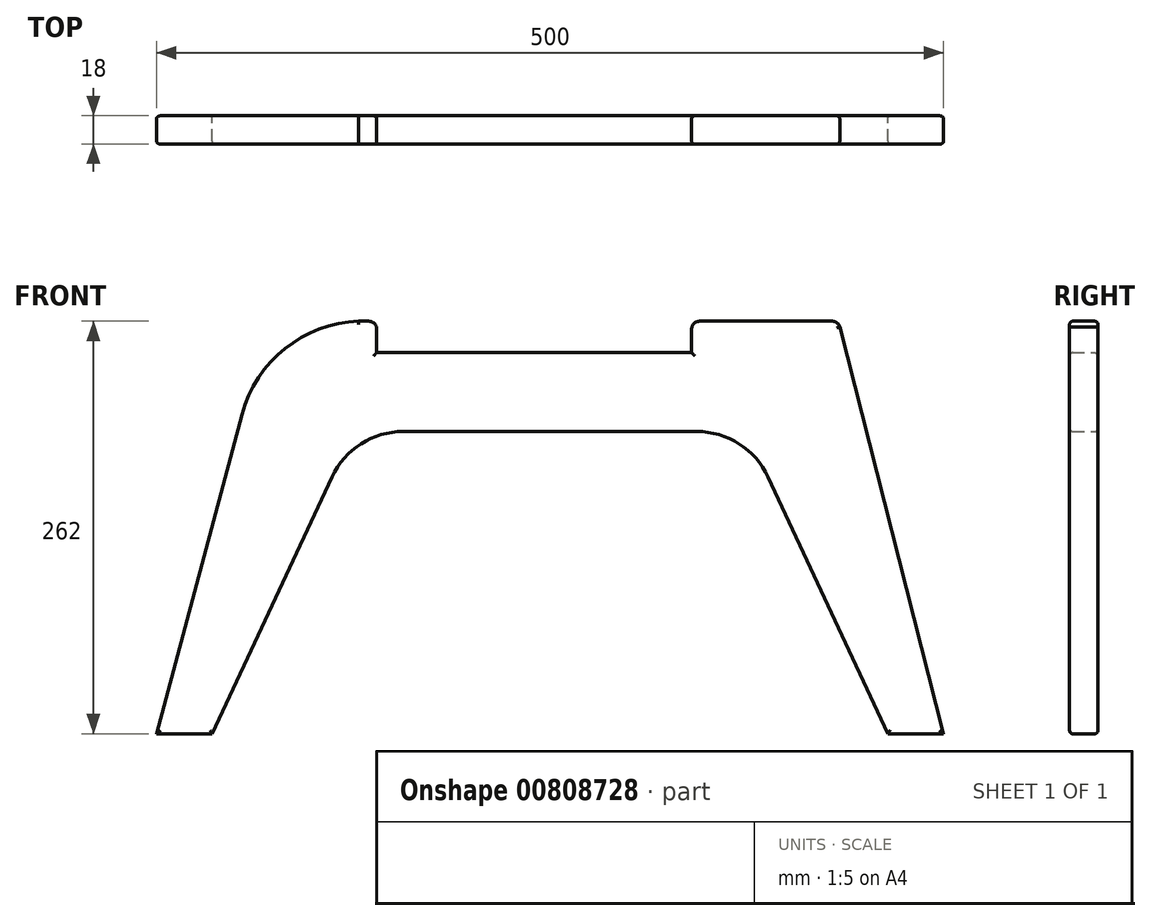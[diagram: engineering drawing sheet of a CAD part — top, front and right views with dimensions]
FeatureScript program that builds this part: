
annotation { "Feature Type Name" : "Feature", "Feature Type Description" : "" }
export const myFeature = defineFeature(function(context is Context, id is Id, definition is map)
    precondition{}
    {
        {
            var Q0;
            Q0=qCreatedBy(makeId("Front.planeOp"),FACE);
            var sketch = newSketch(context, id + "F0", { "sketchPlane" : qUnion([Q0])});
            skLineSegment(sketch, "E0", {"start": v(0, 0) * mm, "end": v(54.33, 202.77) * mm});
            skLineSegment(sketch, "E1", {"start": v(0, 0) * mm, "end": v(35.46, 0) * mm});
            skLineSegment(sketch, "E2", {"start": v(35.46, 0) * mm, "end": v(111.53, 163.13) * mm});
            skArc(sketch, "E3.filletArc", {"start": v(128.37, 262) * mm, "mid": v(81.63, 244.54) * mm, "end": v(54.33, 202.77) * mm});
            skArc(sketch, "E4.filletArc", {"start": v(156.84, 192) * mm, "mid": v(129.98, 184.17) * mm, "end": v(111.53, 163.13) * mm});
            skArc(sketch, "E5.MirrorCS", {"start": v(343.16, 192) * mm, "mid": v(370.02, 184.17) * mm, "end": v(388.47, 163.13) * mm});
            skLineSegment(sketch, "E6.MirrorCS", {"start": v(464.54, 0) * mm, "end": v(388.47, 163.13) * mm});
            skLineSegment(sketch, "E7.MirrorCS", {"start": v(500, 0) * mm, "end": v(464.54, 0) * mm});
            skLineSegment(sketch, "E8", {"start": v(371.63, 262) * mm, "end": v(429.18, 262) * mm});
            skLineSegment(sketch, "E9", {"start": v(128.37, 262) * mm, "end": v(134.92, 262) * mm});
            skLineSegment(sketch, "E10", {"start": v(139.92, 257) * mm, "end": v(139.92, 242) * mm});
            skLineSegment(sketch, "E11", {"start": v(139.92, 242) * mm, "end": v(339.92, 242) * mm});
            skLineSegment(sketch, "E12", {"start": v(339.92, 242) * mm, "end": v(339.92, 257) * mm});
            skLineSegment(sketch, "E13.trimOffspring", {"start": v(344.92, 262) * mm, "end": v(371.63, 262) * mm});
            skPoint(sketch, "E14.visualSharp", {"position": v(139.92, 262) * mm});
            skArc(sketch, "E14.filletArc", {"start": v(139.92, 257) * mm, "mid": v(138.46, 260.54) * mm, "end": v(134.92, 262) * mm});
            skPoint(sketch, "E15.visualSharp", {"position": v(339.92, 262) * mm});
            skArc(sketch, "E15.filletArc", {"start": v(344.92, 262) * mm, "mid": v(341.39, 260.54) * mm, "end": v(339.92, 257) * mm});
            skPoint(sketch, "E16.visualSharp", {"position": v(433.01, 262) * mm});
            skArc(sketch, "E16.filletArc", {"start": v(434, 258.3) * mm, "mid": v(432.22, 260.97) * mm, "end": v(429.18, 262) * mm});
            skLineSegment(sketch, "E17", {"start": v(156.84, 192) * mm, "end": v(343.16, 192) * mm});
            skLineSegment(sketch, "E18", {"start": v(500, 0) * mm, "end": v(434, 258.3) * mm});
            skSolve(sketch);
        }
        {
            var Q0;
            Q0=makeQuery(id+"F0.imprint","IMPRINT",FACE,{"disambiguationData":[TD([[makeQuery(id+"F0.imprint","IMPRINT",EDGE,{"derivedFrom":sQuery(id+"F0.wireOp",EDGE,"E0")}),-1.0]])]});
            extrude(context, id + "F1", {"entities" : qUnion([Q0]), "depth" : 18 * mm, "offsetDistance" : 25 * mm});
        }
        {
            var Q0;
            Q0=makeQuery(id+"F1.opExtrude","CAP_FACE",FACE,{"disambiguationData":[OSD([sQuery(id+"F0.wireOp",EDGE,"E0"),sQuery(id+"F0.wireOp",EDGE,"E1"),sQuery(id+"F0.wireOp",EDGE,"E2"),sQuery(id+"F0.wireOp",EDGE,"MbB4X2aZ-b5OU-bVcF-hZ4d-0ISXhdjHpSIp"),sQuery(id+"F0.wireOp",EDGE,"E3.filletArc"),sQuery(id+"F0.wireOp",EDGE,"E4.filletArc"),sQuery(id+"F0.wireOp",EDGE,"070f1393-5020-4f78-b219-2ca638f1d55b0.MirrorCS"),sQuery(id+"F0.wireOp",EDGE,"E5.MirrorCS"),sQuery(id+"F0.wireOp",EDGE,"E6.MirrorCS"),sQuery(id+"F0.wireOp",EDGE,"E7.MirrorCS"),sQuery(id+"F0.wireOp",EDGE,"5e55f6c9-26e7-4787-a55b-2cd3013a646e0.MirrorCS"),sQuery(id+"F0.wireOp",EDGE,"B95IDqCL-0PlV-wulK-DyKo-xqh16RKUv5Oa"),sQuery(id+"F0.wireOp",EDGE,"E8"),sQuery(id+"F0.wireOp",EDGE,"E9"),sQuery(id+"F0.wireOp",EDGE,"E10"),sQuery(id+"F0.wireOp",EDGE,"E11"),sQuery(id+"F0.wireOp",EDGE,"E12"),sQuery(id+"F0.wireOp",EDGE,"E13.trimOffspring"),sQuery(id+"F0.wireOp",EDGE,"E14.filletArc"),sQuery(id+"F0.wireOp",EDGE,"E15.filletArc"),sQuery(id+"F0.wireOp",EDGE,"E16.filletArc")])],"isStart":false});
            var Q1;
            Q1=makeQuery(id+"F1.opExtrude","CAP_FACE",FACE,{"disambiguationData":[OSD([sQuery(id+"F0.wireOp",EDGE,"E0"),sQuery(id+"F0.wireOp",EDGE,"E1"),sQuery(id+"F0.wireOp",EDGE,"E2"),sQuery(id+"F0.wireOp",EDGE,"MbB4X2aZ-b5OU-bVcF-hZ4d-0ISXhdjHpSIp"),sQuery(id+"F0.wireOp",EDGE,"E3.filletArc"),sQuery(id+"F0.wireOp",EDGE,"E4.filletArc"),sQuery(id+"F0.wireOp",EDGE,"070f1393-5020-4f78-b219-2ca638f1d55b0.MirrorCS"),sQuery(id+"F0.wireOp",EDGE,"E5.MirrorCS"),sQuery(id+"F0.wireOp",EDGE,"E6.MirrorCS"),sQuery(id+"F0.wireOp",EDGE,"E7.MirrorCS"),sQuery(id+"F0.wireOp",EDGE,"5e55f6c9-26e7-4787-a55b-2cd3013a646e0.MirrorCS"),sQuery(id+"F0.wireOp",EDGE,"B95IDqCL-0PlV-wulK-DyKo-xqh16RKUv5Oa"),sQuery(id+"F0.wireOp",EDGE,"E8"),sQuery(id+"F0.wireOp",EDGE,"E9"),sQuery(id+"F0.wireOp",EDGE,"E10"),sQuery(id+"F0.wireOp",EDGE,"E11"),sQuery(id+"F0.wireOp",EDGE,"E12"),sQuery(id+"F0.wireOp",EDGE,"E13.trimOffspring"),sQuery(id+"F0.wireOp",EDGE,"E14.filletArc"),sQuery(id+"F0.wireOp",EDGE,"E15.filletArc"),sQuery(id+"F0.wireOp",EDGE,"E16.filletArc")])],"isStart":true});
            fillet(context, id + "F2", {"entities" : qUnion([Q0, Q1]), "radius" : 2 * mm, "tangentPropagation" : true, "allowEdgeOverflow" : false});
        }
        {
            var Q0;
            Q0=makeQuery(id+"F1.opExtrude","SWEPT_FACE",FACE,{"disambiguationData":[OSD([sQuery(id+"F0.wireOp",EDGE,"E11")])]});
            var sketch = newSketch(context, id + "F3", { "sketchPlane" : qUnion([Q0])});
            skLineSegment(sketch, "E19", {"start": v(139.92, -9) * mm, "end": v(339.92, -9) * mm, "construction": true});
            skPoint(sketch, "E20", {"position": v(239.92, -9) * mm});
            skSolve(sketch);
        }
    });
